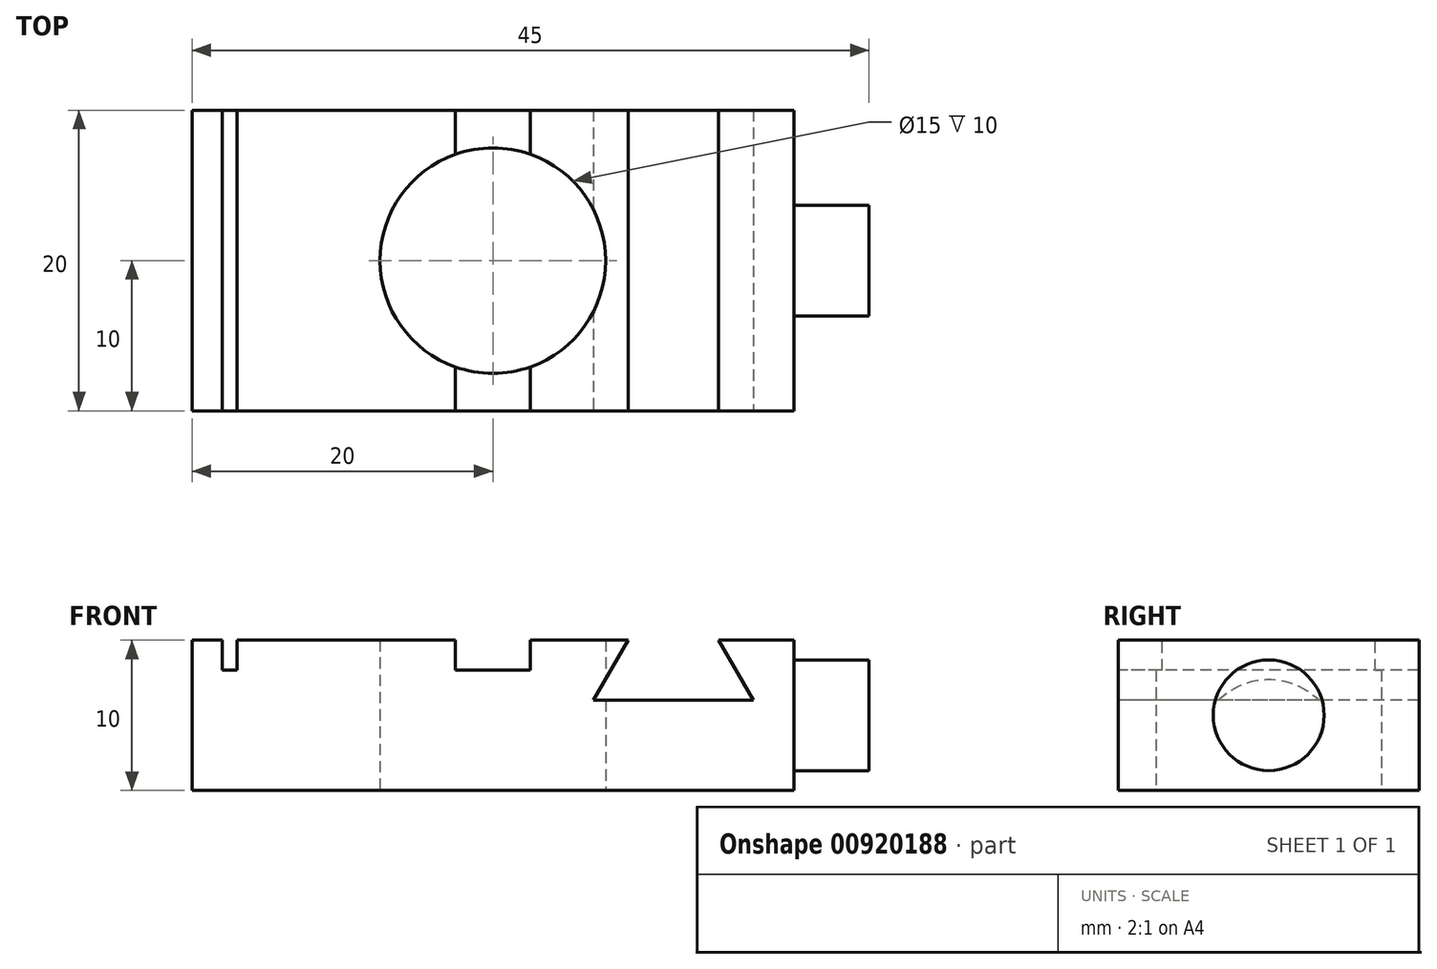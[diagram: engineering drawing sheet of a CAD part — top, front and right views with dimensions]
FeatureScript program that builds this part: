
annotation { "Feature Type Name" : "Feature", "Feature Type Description" : "" }
export const myFeature = defineFeature(function(context is Context, id is Id, definition is map)
    precondition{}
    {
        {
            var Q0;
            Q0=qCreatedBy(makeId("Top.planeOp"),FACE);
            var sketch = newSketch(context, id + "F0", { "sketchPlane" : qUnion([Q0])});
            skLineSegment(sketch, "E0.bottom", {"start": v(-20, 10) * mm, "end": v(20, 10) * mm});
            skLineSegment(sketch, "E0.top", {"start": v(-20, -10) * mm, "end": v(20, -10) * mm});
            skLineSegment(sketch, "E0.left", {"start": v(-20, 10) * mm, "end": v(-20, -10) * mm});
            skLineSegment(sketch, "E0.right", {"start": v(20, 10) * mm, "end": v(20, -10) * mm});
            skPoint(sketch, "E0.middle", {"position": v(0, 0) * mm});
            skCircle(sketch, "E1", {"center": v(0, 0) * mm, "radius": 7.5 * mm});
            skSolve(sketch);
        }
        {
            var Q0;
            Q0=makeQuery(id+"F0.imprint","IMPRINT",FACE,{"disambiguationData":[TD([[makeQuery(id+"F0.imprint","IMPRINT",EDGE,{"derivedFrom":sQuery(id+"F0.wireOp",EDGE,"E0.bottom")}),-1.0]])]});
            extrude(context, id + "F1", {"entities" : qUnion([Q0]), "depth" : 10 * mm, "offsetDistance" : 25 * mm});
        }
        {
            var Q0;
            Q0=makeQuery(id+"F1.opExtrude","CAP_FACE",FACE,{"disambiguationData":[OSD([sQuery(id+"F0.wireOp",EDGE,"E0.bottom"),sQuery(id+"F0.wireOp",EDGE,"E0.top"),sQuery(id+"F0.wireOp",EDGE,"E0.left"),sQuery(id+"F0.wireOp",EDGE,"E0.right"),sQuery(id+"F0.wireOp",EDGE,"E1")])],"isStart":false});
            var sketch = newSketch(context, id + "F2", { "sketchPlane" : qUnion([Q0])});
            skLineSegment(sketch, "E2.bottom", {"start": v(-18, 10) * mm, "end": v(-17, 10) * mm});
            skLineSegment(sketch, "E2.top", {"start": v(-18, -10) * mm, "end": v(-17, -10) * mm});
            skLineSegment(sketch, "E2.left", {"start": v(-18, 10) * mm, "end": v(-18, -10) * mm});
            skLineSegment(sketch, "E2.right", {"start": v(-17, 10) * mm, "end": v(-17, -10) * mm});
            skLineSegment(sketch, "E3", {"start": v(-2.5, 10) * mm, "end": v(-2.5, -10) * mm});
            skLineSegment(sketch, "E4", {"start": v(-2.5, -10) * mm, "end": v(2.5, -10) * mm});
            skLineSegment(sketch, "E5", {"start": v(2.5, -10) * mm, "end": v(2.5, 10) * mm});
            skLineSegment(sketch, "E6", {"start": v(2.5, 10) * mm, "end": v(-2.5, 10) * mm});
            skPoint(sketch, "E7", {"position": v(0, 0) * mm});
            skLineSegment(sketch, "E8", {"start": v(0, 10) * mm, "end": v(0, -10) * mm, "construction": true});
            skSolve(sketch);
        }
        {
            var Q0;
            Q0=makeQuery(id+"F2.imprint","IMPRINT",FACE,{"disambiguationData":[TD([[makeQuery(id+"F2.imprint","IMPRINT",EDGE,{"derivedFrom":sQuery(id+"F2.wireOp",EDGE,"E2.bottom")}),-1.0]])]});
            var Q1;
            {var subQ0=sQuery(id+"F2.wireOp",EDGE,"E4");Q1=makeQuery(id+"F2.imprint","IMPRINT",FACE,{"disambiguationData":[TD([[makeQuery(id+"F2.imprint","IMPRINT",EDGE,{"derivedFrom":subQ0}),1.0]])]});}
            var Q2;
            {var subQ0=sQuery(id+"F2.wireOp",EDGE,"E6");Q2=makeQuery(id+"F2.imprint","IMPRINT",FACE,{"disambiguationData":[TD([[makeQuery(id+"F2.imprint","IMPRINT",EDGE,{"derivedFrom":subQ0}),-1.0]])]});}
            extrude(context, id + "F3", {"entities" : qUnion([Q0, Q1, Q2]), "operationType" : NewBodyOperationType.REMOVE, "oppositeDirection" : true, "depth" : 2 * mm, "offsetDistance" : 25 * mm});
        }
        {
            var Q0;
            Q0=makeQuery(id+"F1.opExtrude","SWEPT_FACE",FACE,{"disambiguationData":[OSD([sQuery(id+"F0.wireOp",EDGE,"E0.top")])]});
            var sketch = newSketch(context, id + "F4", { "sketchPlane" : qUnion([Q0])});
            skLineSegment(sketch, "E9", {"start": v(9, 10) * mm, "end": v(6.7, 6) * mm});
            skLineSegment(sketch, "E10", {"start": v(6.7, 6) * mm, "end": v(17.3, 6) * mm});
            skLineSegment(sketch, "E11", {"start": v(17.3, 6) * mm, "end": v(15, 10) * mm});
            skLineSegment(sketch, "E12", {"start": v(15, 10) * mm, "end": v(9, 10) * mm});
            skLineSegment(sketch, "E13", {"start": v(11.25, 10) * mm, "end": v(11.25, 0) * mm, "construction": true});
            skLineSegment(sketch, "E14", {"start": v(12, 10) * mm, "end": v(12, 0) * mm, "construction": true});
            skPoint(sketch, "E14.endSnap0", {"position": v(12, 6) * mm});
            skSolve(sketch);
        }
        {
            var Q0;
            Q0=makeQuery(id+"F4.imprint","IMPRINT",FACE,{"disambiguationData":[TD([[makeQuery(id+"F4.imprint","IMPRINT",EDGE,{"derivedFrom":sQuery(id+"F4.wireOp",EDGE,"E9")}),1.0]])]});
            extrude(context, id + "F5", {"entities" : qUnion([Q0]), "operationType" : NewBodyOperationType.REMOVE, "endBound" : BoundingType.THROUGH_ALL, "oppositeDirection" : true, "depth" : 25 * mm, "offsetDistance" : 25 * mm});
        }
        {
            var Q0;
            Q0=makeQuery(id+"F1.opExtrude","SWEPT_FACE",FACE,{"disambiguationData":[OSD([sQuery(id+"F0.wireOp",EDGE,"E0.right")])]});
            var sketch = newSketch(context, id + "F6", { "sketchPlane" : qUnion([Q0])});
            skCircle(sketch, "E15", {"center": v(0, 5) * mm, "radius": 3.68 * mm});
            skPoint(sketch, "E15.centerSnap0", {"position": v(-10, 5) * mm});
            skPoint(sketch, "E15.centerSnap1", {"position": v(0, 10) * mm});
            skSolve(sketch);
        }
        {
            var Q0;
            Q0=makeQuery(id+"F6.imprint","IMPRINT",FACE,{"disambiguationData":[TD([[makeQuery(id+"F6.imprint","IMPRINT",EDGE,{"derivedFrom":sQuery(id+"F6.wireOp",EDGE,"E15")}),1.0]])]});
            extrude(context, id + "F7", {"entities" : qUnion([Q0]), "operationType" : NewBodyOperationType.ADD, "depth" : 5 * mm, "offsetDistance" : 25 * mm});
        }
    });
